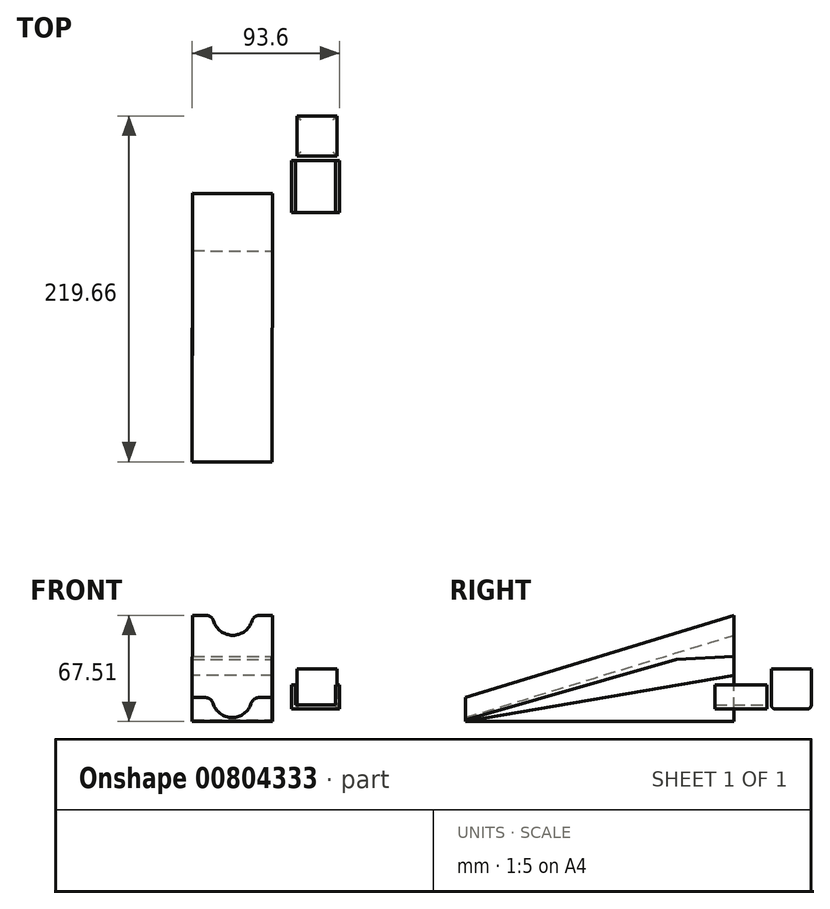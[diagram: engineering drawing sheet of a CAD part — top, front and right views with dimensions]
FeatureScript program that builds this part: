
annotation { "Feature Type Name" : "Feature", "Feature Type Description" : "" }
export const myFeature = defineFeature(function(context is Context, id is Id, definition is map)
    precondition{}
    {
        {
            var Q0;
            Q0=qCreatedBy(makeId("Front.planeOp"),FACE);
            var sketch = newSketch(context, id + "F0", { "sketchPlane" : qUnion([Q0])});
            skLineSegment(sketch, "E0", {"start": v(-46.34, 59.55) * mm, "end": v(-33.64, 59.55) * mm});
            skArc(sketch, "E1", {"start": v(-33.64, 59.55) * mm, "mid": v(-20.94, 46.85) * mm, "end": v(-8.24, 59.55) * mm});
            skLineSegment(sketch, "E2", {"start": v(-8.24, 59.55) * mm, "end": v(4.46, 59.55) * mm});
            skLineSegment(sketch, "E3", {"start": v(4.46, 59.55) * mm, "end": v(4.46, 21.45) * mm});
            skLineSegment(sketch, "E4", {"start": v(4.46, 21.45) * mm, "end": v(-46.34, 21.45) * mm});
            skLineSegment(sketch, "E5", {"start": v(-46.34, 21.45) * mm, "end": v(-46.34, 59.55) * mm});
            skSolve(sketch);
        }
        {
            var Q0;
            Q0=qCreatedBy(makeId("Front.planeOp"),FACE);
            cPlane(context, id + "F1", {"entities" : qUnion([Q0]), "cplaneType" : CPlaneType.OFFSET, "offset" : 63.5 * mm, "width" : 152.4 * mm, "height" : 152.4 * mm});
        }
        {
            var Q0;
            Q0=qCreatedBy(id+"F1.planeOp",FACE);
            cPlane(context, id + "F2", {"entities" : qUnion([Q0]), "cplaneType" : CPlaneType.OFFSET, "offset" : 106.93 * mm, "width" : 152.4 * mm, "height" : 152.4 * mm});
        }
        {
            var Q0;
            Q0=qCreatedBy(id+"F2.planeOp",FACE);
            var sketch = newSketch(context, id + "F3", { "sketchPlane" : qUnion([Q0])});
            skLineSegment(sketch, "E6", {"start": v(-46.72, 7.28) * mm, "end": v(-34.02, 7.28) * mm});
            skArc(sketch, "E7", {"start": v(-34.02, 7.28) * mm, "mid": v(-21.32, -5.42) * mm, "end": v(-8.62, 7.28) * mm});
            skLineSegment(sketch, "E8", {"start": v(-8.62, 7.28) * mm, "end": v(4.08, 7.28) * mm});
            skLineSegment(sketch, "E9", {"start": v(4.08, 7.28) * mm, "end": v(4.08, -7.96) * mm});
            skLineSegment(sketch, "E10", {"start": v(4.08, -7.96) * mm, "end": v(-46.72, -7.96) * mm});
            skLineSegment(sketch, "E11", {"start": v(-46.72, -7.96) * mm, "end": v(-46.72, 7.28) * mm});
            skSolve(sketch);
        }
        {
            var Q0;
            Q0=makeQuery(id+"F0.imprint","IMPRINT",FACE,{"disambiguationData":[TD([[makeQuery(id+"F0.imprint","IMPRINT",EDGE,{"derivedFrom":sQuery(id+"F0.wireOp",EDGE,"E0")}),-1.0]])]});
            var Q1;
            Q1=makeQuery(id+"F3.imprint","IMPRINT",FACE,{"disambiguationData":[TD([[makeQuery(id+"F3.imprint","IMPRINT",EDGE,{"derivedFrom":sQuery(id+"F3.wireOp",EDGE,"E6")}),-1.0]])]});
            loft(context, id + "F4", {"sheetProfilesArray" : [{ "sheetProfileEntities" : qUnion([Q0]) }, { "sheetProfileEntities" : qUnion([Q1]) }]});
        }
        {
            var Q0;
            Q0=makeQuery(id+"F4.opLoft","SWEPT_EDGE",EDGE,{"disambiguationData":[OSD([sQuery(id+"F0.wireOp",EDGE,"E0"),sQuery(id+"F0.wireOp",EDGE,"E1"),sQuery(id+"F3.wireOp",EDGE,"E6"),sQuery(id+"F3.wireOp",EDGE,"E7")])]});
            var Q1;
            Q1=makeQuery(id+"F4.opLoft","SWEPT_EDGE",EDGE,{"disambiguationData":[OSD([sQuery(id+"F0.wireOp",EDGE,"E1"),sQuery(id+"F0.wireOp",EDGE,"E2"),sQuery(id+"F3.wireOp",EDGE,"E7"),sQuery(id+"F3.wireOp",EDGE,"E8")])]});
            fillet(context, id + "F5", {"entities" : qUnion([Q0, Q1]), "radius" : 5.08 * mm, "tangentPropagation" : true, "allowEdgeOverflow" : false});
        }
        {
            var Q0;
            Q0=makeQuery(id+"F4.opLoft","SWEPT_FACE",FACE,{"disambiguationData":[OSD([sQuery(id+"F0.wireOp",EDGE,"E2"),sQuery(id+"F0.wireOp",EDGE,"E3"),sQuery(id+"F0.wireOp",EDGE,"E4"),sQuery(id+"F3.wireOp",EDGE,"E8"),sQuery(id+"F3.wireOp",EDGE,"E9"),sQuery(id+"F3.wireOp",EDGE,"E10")])]});
            var sketch = newSketch(context, id + "F6", { "sketchPlane" : qUnion([Q0])});
            skLineSegment(sketch, "E12", {"start": v(-170.42, -7.96) * mm, "end": v(0, -7.96) * mm});
            skLineSegment(sketch, "E13", {"start": v(0, -7.96) * mm, "end": v(0.01, 33.33) * mm});
            skLineSegment(sketch, "E14", {"start": v(0.01, 33.33) * mm, "end": v(-36.5, 31.65) * mm});
            skLineSegment(sketch, "E15", {"start": v(-170.42, -7.96) * mm, "end": v(-170.42, -6.81) * mm});
            skLineSegment(sketch, "E16", {"start": v(-170.42, -6.81) * mm, "end": v(-36.5, 31.65) * mm});
            skSolve(sketch);
        }
        {
            var Q0;
            Q0 = qSketchRegion(id + "F6", true);
            extrude(context, id + "F7", {"entities" : qUnion([Q0]), "oppositeDirection" : true, "depth" : 50.8 * mm, "offsetDistance" : 25.4 * mm});
        }
        {
            var Q0;
            Q0=qCreatedBy(makeId("Top.planeOp"),FACE);
            var sketch = newSketch(context, id + "F8", { "sketchPlane" : qUnion([Q0])});
            skLineSegment(sketch, "E17.bottom", {"start": v(19.77, 49.23) * mm, "end": v(45.17, 49.23) * mm});
            skLineSegment(sketch, "E17.top", {"start": v(19.77, 23.83) * mm, "end": v(45.17, 23.83) * mm});
            skLineSegment(sketch, "E17.left", {"start": v(19.77, 49.23) * mm, "end": v(19.77, 23.83) * mm});
            skLineSegment(sketch, "E17.right", {"start": v(45.17, 49.23) * mm, "end": v(45.17, 23.83) * mm});
            skSolve(sketch);
        }
        {
            var Q0;
            Q0 = qSketchRegion(id + "F8", true);
            extrude(context, id + "F9", {"entities" : qUnion([Q0]), "depth" : 25.4 * mm, "offsetDistance" : 25.4 * mm});
        }
        {
            var Q0;
            Q0=makeQuery(id+"F9.opExtrude","CAP_EDGE",EDGE,{"disambiguationData":[OSD([sQuery(id+"F8.wireOp",EDGE,"E17.top")])],"isStart":true});
            var Q1;
            Q1=makeQuery(id+"F9.opExtrude","CAP_EDGE",EDGE,{"disambiguationData":[OSD([sQuery(id+"F8.wireOp",EDGE,"E17.right")])],"isStart":true});
            var Q2;
            Q2=makeQuery(id+"F9.opExtrude","CAP_EDGE",EDGE,{"disambiguationData":[OSD([sQuery(id+"F8.wireOp",EDGE,"E17.left")])],"isStart":true});
            var Q3;
            Q3=makeQuery(id+"F9.opExtrude","CAP_EDGE",EDGE,{"disambiguationData":[OSD([sQuery(id+"F8.wireOp",EDGE,"E17.bottom")])],"isStart":true});
            fillet(context, id + "F10", {"entities" : qUnion([Q0, Q1, Q2, Q3]), "radius" : 2.54 * mm, "tangentPropagation" : true, "allowEdgeOverflow" : false});
        }
        {
            var Q0;
            Q0=qCreatedBy(makeId("Top.planeOp"),FACE);
            var sketch = newSketch(context, id + "F11", { "sketchPlane" : qUnion([Q0])});
            skLineSegment(sketch, "E18", {"start": v(16.4, 21) * mm, "end": v(46.88, 21) * mm});
            skLineSegment(sketch, "E19", {"start": v(16.4, 21) * mm, "end": v(16.4, -12.01) * mm});
            skLineSegment(sketch, "E20", {"start": v(46.88, 21) * mm, "end": v(46.88, -12.01) * mm});
            skLineSegment(sketch, "E21", {"start": v(16.4, -12.01) * mm, "end": v(46.88, -12.01) * mm});
            skSolve(sketch);
        }
        {
            var Q0;
            Q0 = qSketchRegion(id + "F11", true);
            extrude(context, id + "F12", {"entities" : qUnion([Q0]), "depth" : 2.54 * mm, "offsetDistance" : 25.4 * mm});
        }
        {
            var Q0;
            Q0=makeQuery(id+"F12.opExtrude","CAP_FACE",FACE,{"disambiguationData":[OSD([sQuery(id+"F11.wireOp",EDGE,"E18"),sQuery(id+"F11.wireOp",EDGE,"E19"),sQuery(id+"F11.wireOp",EDGE,"E20"),sQuery(id+"F11.wireOp",EDGE,"E21")])],"isStart":false});
            var sketch = newSketch(context, id + "F13", { "sketchPlane" : qUnion([Q0])});
            skLineSegment(sketch, "E22", {"start": v(16.4, -12.01) * mm, "end": v(18.95, -12.01) * mm});
            skLineSegment(sketch, "E23", {"start": v(18.95, -12.01) * mm, "end": v(18.95, 21) * mm});
            skLineSegment(sketch, "E24", {"start": v(18.95, 21) * mm, "end": v(16.4, 21) * mm});
            skLineSegment(sketch, "E25", {"start": v(16.4, 21) * mm, "end": v(16.4, -12.01) * mm});
            skLineSegment(sketch, "E26", {"start": v(46.88, 21) * mm, "end": v(46.88, -12.01) * mm});
            skLineSegment(sketch, "E27", {"start": v(46.88, -12.01) * mm, "end": v(44.34, -12.01) * mm});
            skLineSegment(sketch, "E28", {"start": v(44.34, -12.01) * mm, "end": v(44.34, 21) * mm});
            skLineSegment(sketch, "E29", {"start": v(44.34, 21) * mm, "end": v(46.88, 21) * mm});
            skSolve(sketch);
        }
        {
            var Q0;
            Q0 = qSketchRegion(id + "F13", true);
            extrude(context, id + "F14", {"entities" : qUnion([Q0]), "operationType" : NewBodyOperationType.ADD, "depth" : 12.7 * mm, "offsetDistance" : 25.4 * mm});
        }
    });
